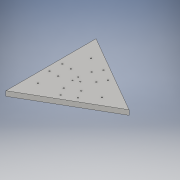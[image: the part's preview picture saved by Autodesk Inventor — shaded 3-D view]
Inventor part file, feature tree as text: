
AUTODESK INVENTOR PART (.ipt)
format: ipt  version: 2016 (Build 200138000, 138)  size: 187,904 bytes
history: native  units: in
note: dims shown in document units (in); Inventor stores cm internally (conversion verified against a paired STEP export)
features: extrude x6, sketch x6
ambient origin geometry x8: Origin, YZ Plane, XZ Plane, XY Plane, X Axis, Y Axis, Z Axis, Center Point
bodies: Solid1 (feature_tree)
feature tree (12):
  extrude  "TriangleFace"  Depth=11.1024in
  extrude  "SideTwoHoles"  Depth=0.5906in
  extrude  "SideOneHoles"  Depth=0.7874in
  extrude  "SideThreeHoles"  Depth=0.7874in
  extrude  "CenterHoles"  Depth=0.1575in
  extrude  "Extrusion7"  Depth=0.5906in
  sketch  "Sketch1"  dims[d0=3.5433in d1=11.1024in]
  sketch  "Sketch2"  dims[d2=0.5906in d3=0.0in d4=0.6102in]
  sketch  "Sketch3"  dims[d5=0.7874in d6=0.7874in]
  sketch  "Sketch4"  dims[d7=1.063in d8=0.7874in]
  sketch  "Sketch5"  dims[d9=0.7874in d10=0.1575in]
  sketch  "Sketch6"  dims[d11=0.1575in d12=0.1575in d13=0.1575in d14=0.5906in d15=0.0in d16=0.6102in d17=1.063in d18=0.7874in d19=0.7874in d20=0.7874in d21=0.7874in d22=0.1575in d23=0.1575in d24=0.1575in d25=0.1575in d26=0.5906in d27=0.0in d28=0.6102in d29=1.063in d30=0.7874in d31=0.7874in d32=0.7874in d33=0.7874in d34=0.1575in d35=0.1575in d36=0.1575in d37=0.1575in d38=0.5906in d39=0.0in d40=1.1811in d43=0.2756in d44=60.0deg d45=0.1378in d46=0.2756in d47=60.0deg d48=0.1378in d49=0.2756in d50=180.0deg d51=0.1378in d52=0.5906in d53=0.0in d54=2.7559in d55=1.1811in d56=0.0in d57=0.1575in d60=2.7559in d61=1.1811in d62=2.7559in d63=1.1811in d64=0.1575in d65=0.1575in d66=0.5906in d67=0.0in]
